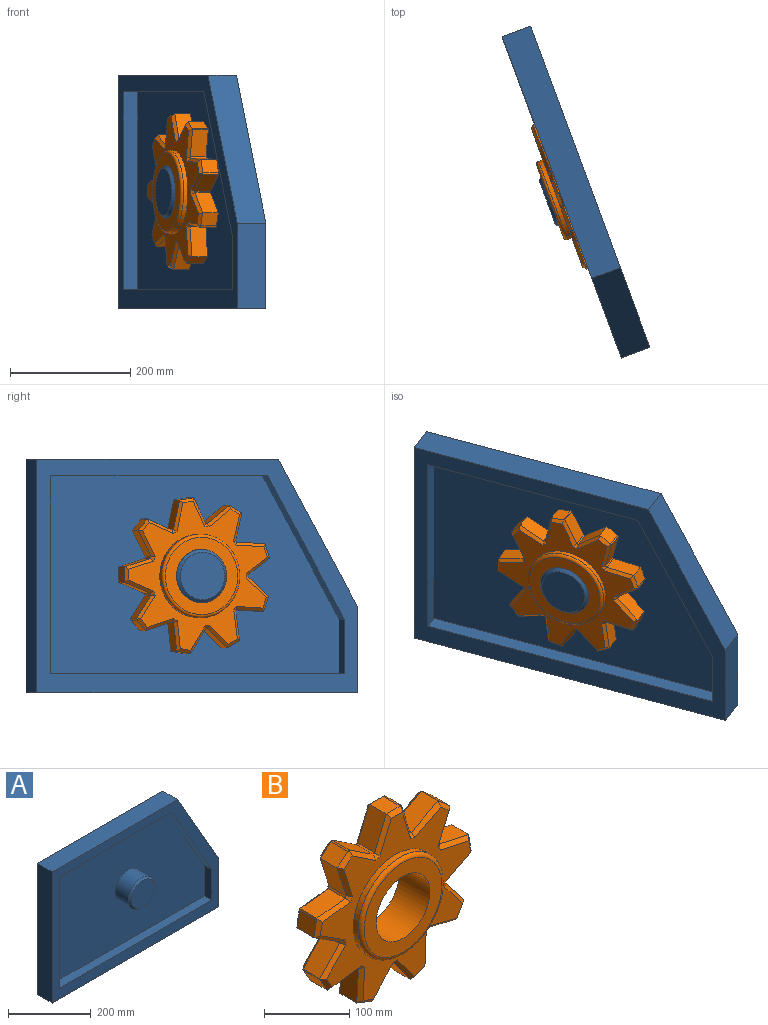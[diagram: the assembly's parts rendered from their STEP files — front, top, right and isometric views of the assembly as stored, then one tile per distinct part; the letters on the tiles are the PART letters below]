
ASSEMBLY  parts=2 mates=1
PART A: 16 faces, bbox 569.8x76.2x388.2 mm
  f0: plane 569.83x388.19mm, normal (0,1,0), area 203883.7mm2, adj f6,f7,f8,f9,f10
  f1: plane 384.89x25.4mm, normal (0,0,-1), area 9776.1mm2, adj f2,f5,f11,f12
  f2: plane 329.12x25.4mm, normal (1,0,0), area 8359.7mm2, adj f1,f3,f11,f12
  f3: plane 521.46x25.4mm, normal (0,0,1), area 13245.1mm2, adj f2,f4,f11,f12
  f4: plane 90.86x25.4mm, normal (-1,0,0), area 2307.9mm2, adj f3,f5,f11,f12
  f5: plane 238.26x136.58mm, normal (-0.87,0,-0.5), area 6975.6mm2, adj f1,f4,f11,f12
  f6: plane 428.93x50.8mm, normal (0,0,1), area 21789.7mm2, adj f0,f7,f10,f11
  f7: plane 388.19x50.8mm, normal (-1,0,0), area 19719.8mm2, adj f0,f6,f8,f11
  f8: plane 569.83x50.8mm, normal (0,0,-1), area 28947.5mm2, adj f0,f7,f9,f11
  f9: plane 142.38x50.8mm, normal (1,0,0), area 7233mm2, adj f0,f8,f10,f11
  f10: plane 245.8x140.9mm, normal (0.87,0,0.5), area 14392.8mm2, adj f0,f6,f9,f11
  f11: plane 569.83x388.19mm, normal (0,-1,0), area 48530.3mm2, adj f1,f2,f3,f4,f5,f6,f7,f8
  f12: plane 521.46x329.12mm, normal (0,-1,0), area 149146.3mm2, adj f1,f2,f3,f4,f5,f13
  f13: cylinder r=44.45mm len=88.9mm, axis (0,1,0), area 12769mm2, adj f12,f15
  f14: plane 78.74x78.74mm, normal (0,-1,0), area 4869.5mm2, adj f15
  f15: cone r=39.37mm half-angle=45deg, axis (0,1,0), area 1891.8mm2, adj f13,f14
PART B: 123 faces, bbox 260x50.8x257 mm
  f0: cylinder r=88.9mm len=27.94mm, axis (0,1,0), area 84mm2, adj f1,f44,f71,f107
  f1: plane 42.39x27.94mm, normal (0.45,0,-0.89), area 1323.4mm2, adj f0,f2,f73,f109
  f2: cylinder r=130.4mm len=28.36mm, axis (0,1,0), area 67.7mm2, adj f1,f3,f73,f75,f109,f111
  f3: plane 27.94x22.84mm, normal (0.99,0,0.16), area 646.6mm2, adj f2,f4,f75,f111
  f4: plane 48.59x27.94mm, normal (0.22,0,0.98), area 1390.3mm2, adj f3,f5,f77,f113
  f5: cylinder r=88.9mm len=27.94mm, axis (0,1,0), area 84mm2, adj f4,f6,f79,f115
  f6: plane 43.44x27.94mm, normal (0.92,0,-0.4), area 1323.4mm2, adj f5,f7,f81,f117
  f7: cylinder r=130.4mm len=28.36mm, axis (0,1,0), area 67.7mm2, adj f6,f8,f81,f82,f117,f118
  f8: plane 27.94x17.55mm, normal (0.65,0,0.76), area 646.6mm2, adj f7,f9,f82,f118
  f9: plane 44.11x27.94mm, normal (-0.46,0,0.89), area 1390.3mm2, adj f8,f10,f80,f116
  f10: cylinder r=88.9mm len=27.94mm, axis (0,1,0), area 84mm2, adj f9,f11,f78,f114
  f11: plane 45.42x27.94mm, normal (0.96,0,0.28), area 1323.4mm2, adj f10,f12,f76,f112
  f12: cylinder r=130.4mm len=28.36mm, axis (0,1,0), area 67.7mm2, adj f11,f13,f74,f76,f110,f112
  f13: plane 27.94x23.14mm, normal (0.01,0,1), area 646.6mm2, adj f12,f14,f74,f110
  f14: plane 45.99x27.94mm, normal (-0.92,0,0.38), area 1390.3mm2, adj f13,f15,f72,f108
  f15: cylinder r=88.9mm len=27.94mm, axis (0,1,0), area 84mm2, adj f14,f16,f70,f106
  f16: plane 39.5x27.94mm, normal (0.55,0,0.83), area 1323.4mm2, adj f15,f17,f68,f104
  f17: cylinder r=130.4mm len=28.36mm, axis (0,1,0), area 67.7mm2, adj f16,f18,f66,f68,f102,f104
  f18: plane 27.94x17.9mm, normal (-0.63,0,0.77), area 646.6mm2, adj f17,f19,f66,f102
  f19: plane 47.44x27.94mm, normal (-0.95,0,-0.3), area 1390.3mm2, adj f18,f20,f64,f100
  f20: cylinder r=88.9mm len=27.94mm, axis (0,1,0), area 84mm2, adj f19,f21,f62,f98
  f21: plane 47.06x27.94mm, normal (-0.11,0,0.99), area 1323.4mm2, adj f20,f22,f60,f96
  f22: cylinder r=130.4mm len=28.36mm, axis (0,1,0), area 67.7mm2, adj f21,f23,f58,f60,f94,f96
  f23: plane 27.94x22.74mm, normal (-0.98,0,0.19), area 646.6mm2, adj f22,f24,f58,f94
  f24: plane 41.99x27.94mm, normal (-0.54,0,-0.84), area 1390.3mm2, adj f23,f25,f56,f92
  f25: cylinder r=88.9mm len=27.94mm, axis (0,1,0), area 84mm2, adj f24,f26,f54,f90
  f26: plane 34.36x32.61mm, normal (-0.73,0,0.69), area 1323.4mm2, adj f25,f27,f52,f88
  f27: cylinder r=130.4mm len=28.36mm, axis (0,1,0), area 67.7mm2, adj f26,f28,f50,f52,f86,f88
  f28: plane 27.94x20.18mm, normal (-0.87,0,-0.49), area 646.6mm2, adj f27,f29,f50,f86
  f29: plane 49.33x27.94mm, normal (0.13,0,-0.99), area 1390.3mm2, adj f28,f30,f48,f84
  f30: cylinder r=88.9mm len=27.94mm, axis (0,1,0), area 84mm2, adj f29,f31,f47,f83
  f31: plane 47.28x27.94mm, normal (-1,0,0.06), area 1323.4mm2, adj f30,f32,f49,f85
  f32: cylinder r=130.4mm len=28.36mm, axis (0,1,0), area 67.7mm2, adj f31,f33,f49,f51,f85,f87
  f33: plane 27.94x21.65mm, normal (-0.35,0,-0.94), area 646.6mm2, adj f32,f34,f51,f87
  f34: plane 36.72x33.58mm, normal (0.74,0,-0.67), area 1390.3mm2, adj f33,f35,f53,f89
  f35: cylinder r=88.9mm len=27.94mm, axis (0,1,0), area 84mm2, adj f34,f36,f55,f91
  f36: plane 38.08x28.17mm, normal (-0.8,0,-0.59), area 1323.4mm2, adj f35,f37,f57,f93
  f37: cylinder r=130.4mm len=28.36mm, axis (0,1,0), area 67.7mm2, adj f36,f38,f57,f59,f93,f95
  f38: plane 27.94x21.84mm, normal (0.33,0,-0.94), area 646.6mm2, adj f37,f39,f59,f95
  f39: plane 49.71x27.94mm, normal (1,0,-0.04), area 1390.3mm2, adj f38,f40,f61,f97
  f40: cylinder r=88.9mm len=27.94mm, axis (0,1,0), area 84mm2, adj f39,f41,f63,f99
  f41: plane 46.06x27.94mm, normal (-0.23,0,-0.97), area 1323.4mm2, adj f40,f42,f65,f101
  f42: cylinder r=130.4mm len=28.36mm, axis (0,1,0), area 67.7mm2, adj f41,f43,f65,f67,f101,f103
  f43: plane 27.94x19.91mm, normal (0.86,0,-0.51), area 646.6mm2, adj f42,f44,f67,f103
  f44: plane 39.45x30.33mm, normal (0.79,0,0.61), area 1390.3mm2, adj f0,f43,f69,f105
  f45: plane 248.95x246.02mm, normal (0,-1,0), area 19557.7mm2, adj f47,f48,f49,f50,f51,f52,f53,f54
  f46: plane 248.95x246.02mm, normal (0,1,0), area 28484.4mm2, adj f83,f84,f85,f86,f87,f88,f89,f90
  f47: cone r=83.82mm half-angle=45deg, axis (0,1,0), area 38.5mm2, adj f30,f45,f48,f49
  f48: plane 50.97x11.89mm, normal (0.09,-0.71,-0.7), area 353.4mm2, adj f29,f45,f47,f50
  f49: plane 49.73x8.13mm, normal (-0.71,-0.71,0.04), area 338.1mm2, adj f31,f32,f45,f47,f51
  f50: plane 22.18x14.97mm, normal (-0.62,-0.71,-0.35), area 156.8mm2, adj f27,f28,f45,f48,f52
  f51: plane 23.61x12.43mm, normal (-0.25,-0.71,-0.66), area 156.8mm2, adj f32,f33,f45,f49,f53
  f52: plane 38.13x35.31mm, normal (-0.51,-0.71,0.49), area 338.1mm2, adj f26,f27,f45,f50,f54
  f53: plane 41.87x35.01mm, normal (0.52,-0.71,-0.48), area 353.4mm2, adj f34,f45,f51,f55
  f54: cone r=83.82mm half-angle=45deg, axis (0,1,0), area 38.5mm2, adj f25,f45,f52,f56
  f55: cone r=83.82mm half-angle=45deg, axis (0,1,0), area 38.5mm2, adj f35,f45,f53,f57
  f56: plane 46.68x29.13mm, normal (-0.38,-0.71,-0.6), area 353.4mm2, adj f24,f45,f54,f58
  f57: plane 43.24x30.17mm, normal (-0.57,-0.71,-0.42), area 338.1mm2, adj f36,f37,f45,f55,f59
  f58: plane 24.84x9.02mm, normal (-0.69,-0.71,0.13), area 156.8mm2, adj f22,f23,f45,f56,f60
  f59: plane 23.96x11.84mm, normal (0.23,-0.71,-0.67), area 156.8mm2, adj f37,f38,f45,f57,f61
  f60: plane 50.35x10.01mm, normal (-0.08,-0.71,0.7), area 338.1mm2, adj f21,f22,f45,f58,f62
  f61: plane 52.26x7.05mm, normal (0.71,-0.71,-0.03), area 353.4mm2, adj f39,f45,f59,f63
  f62: cone r=83.82mm half-angle=45deg, axis (0,1,0), area 38.5mm2, adj f20,f45,f60,f64
  f63: cone r=83.82mm half-angle=45deg, axis (0,1,0), area 38.5mm2, adj f40,f45,f61,f65
  f64: plane 48.13x20.56mm, normal (-0.67,-0.71,-0.21), area 353.4mm2, adj f19,f45,f62,f66
  f65: plane 47.6x16.62mm, normal (-0.17,-0.71,-0.69), area 338.1mm2, adj f41,f42,f45,f63,f67
  f66: plane 20.03x17.63mm, normal (-0.45,-0.71,0.55), area 156.8mm2, adj f17,f18,f45,f64,f68
  f67: plane 21.67x15.46mm, normal (0.61,-0.71,-0.36), area 156.8mm2, adj f42,f43,f45,f65,f69
  f68: plane 39.69x31.85mm, normal (0.39,-0.71,0.59), area 338.1mm2, adj f16,f17,f45,f66,f70
  f69: plane 39.81x35.78mm, normal (0.56,-0.71,0.43), area 353.4mm2, adj f44,f45,f67,f71
  f70: cone r=83.82mm half-angle=45deg, axis (0,1,0), area 38.5mm2, adj f15,f45,f68,f72
  f71: cone r=83.82mm half-angle=45deg, axis (0,1,0), area 38.5mm2, adj f0,f45,f69,f73
  f72: plane 50.08x22.38mm, normal (-0.65,-0.71,0.27), area 353.4mm2, adj f14,f45,f70,f74
  f73: plane 47.04x24.12mm, normal (0.32,-0.71,-0.63), area 338.1mm2, adj f1,f2,f45,f71,f75
  f74: plane 25.31x5.34mm, normal (0.01,-0.71,0.71), area 156.8mm2, adj f12,f13,f45,f72,f76
  f75: plane 25.02x8.36mm, normal (0.7,-0.71,0.11), area 156.8mm2, adj f2,f3,f45,f73,f77
  f76: plane 49.44x17.33mm, normal (0.68,-0.71,0.2), area 338.1mm2, adj f11,f12,f45,f74,f78
  f77: plane 51.96x14.94mm, normal (0.15,-0.71,0.69), area 353.4mm2, adj f4,f45,f75,f79
  f78: cone r=83.82mm half-angle=45deg, axis (0,1,0), area 38.5mm2, adj f10,f45,f76,f80
  f79: cone r=83.82mm half-angle=45deg, axis (0,1,0), area 38.5mm2, adj f5,f45,f77,f81
  f80: plane 44.11x28.6mm, normal (-0.33,-0.71,0.63), area 353.4mm2, adj f9,f45,f78,f82
  f81: plane 44.02x24.61mm, normal (0.65,-0.71,-0.28), area 338.1mm2, adj f6,f7,f45,f79,f82
  f82: plane 19.77x18.01mm, normal (0.46,-0.71,0.54), area 156.8mm2, adj f7,f8,f45,f80,f81
  f83: cone r=88.9mm half-angle=45deg, axis (0,-1,0), area 38.5mm2, adj f30,f46,f84,f85
  f84: plane 50.97x11.89mm, normal (0.09,0.71,-0.7), area 353.4mm2, adj f29,f46,f83,f86
  f85: plane 49.73x8.13mm, normal (-0.71,0.71,0.04), area 338.1mm2, adj f31,f32,f46,f83,f87
  f86: plane 22.18x14.97mm, normal (-0.62,0.71,-0.35), area 156.8mm2, adj f27,f28,f46,f84,f88
  f87: plane 23.61x12.43mm, normal (-0.25,0.71,-0.66), area 156.8mm2, adj f32,f33,f46,f85,f89
  f88: plane 38.13x35.31mm, normal (-0.51,0.71,0.49), area 338.1mm2, adj f26,f27,f46,f86,f90
  f89: plane 41.87x35.01mm, normal (0.52,0.71,-0.48), area 353.4mm2, adj f34,f46,f87,f91
  f90: cone r=88.9mm half-angle=45deg, axis (0,-1,0), area 38.5mm2, adj f25,f46,f88,f92
  f91: cone r=88.9mm half-angle=45deg, axis (0,-1,0), area 38.5mm2, adj f35,f46,f89,f93
  f92: plane 46.68x29.13mm, normal (-0.38,0.71,-0.6), area 353.4mm2, adj f24,f46,f90,f94
  f93: plane 43.24x30.17mm, normal (-0.57,0.71,-0.42), area 338.1mm2, adj f36,f37,f46,f91,f95
  f94: plane 24.84x9.02mm, normal (-0.69,0.71,0.13), area 156.8mm2, adj f22,f23,f46,f92,f96
  f95: plane 23.96x11.84mm, normal (0.23,0.71,-0.67), area 156.8mm2, adj f37,f38,f46,f93,f97
  f96: plane 50.35x10.01mm, normal (-0.08,0.71,0.7), area 338.1mm2, adj f21,f22,f46,f94,f98
  f97: plane 52.26x7.05mm, normal (0.71,0.71,-0.03), area 353.4mm2, adj f39,f46,f95,f99
  f98: cone r=88.9mm half-angle=45deg, axis (0,-1,0), area 38.5mm2, adj f20,f46,f96,f100
  f99: cone r=88.9mm half-angle=45deg, axis (0,-1,0), area 38.5mm2, adj f40,f46,f97,f101
  f100: plane 48.13x20.56mm, normal (-0.67,0.71,-0.21), area 353.4mm2, adj f19,f46,f98,f102
  f101: plane 47.6x16.62mm, normal (-0.17,0.71,-0.69), area 338.1mm2, adj f41,f42,f46,f99,f103
  f102: plane 20.03x17.63mm, normal (-0.45,0.71,0.55), area 156.8mm2, adj f17,f18,f46,f100,f104
  f103: plane 21.67x15.46mm, normal (0.61,0.71,-0.36), area 156.8mm2, adj f42,f43,f46,f101,f105
  f104: plane 39.69x31.85mm, normal (0.39,0.71,0.59), area 338.1mm2, adj f16,f17,f46,f102,f106
  f105: plane 39.81x35.78mm, normal (0.56,0.71,0.43), area 353.4mm2, adj f44,f46,f103,f107
  f106: cone r=88.9mm half-angle=45deg, axis (0,-1,0), area 38.5mm2, adj f15,f46,f104,f108
  f107: cone r=88.9mm half-angle=45deg, axis (0,-1,0), area 38.5mm2, adj f0,f46,f105,f109
  f108: plane 50.08x22.38mm, normal (-0.65,0.71,0.27), area 353.4mm2, adj f14,f46,f106,f110
  f109: plane 47.04x24.12mm, normal (0.32,0.71,-0.63), area 338.1mm2, adj f1,f2,f46,f107,f111
  f110: plane 25.31x5.34mm, normal (0.01,0.71,0.71), area 156.8mm2, adj f12,f13,f46,f108,f112
  f111: plane 25.02x8.36mm, normal (0.7,0.71,0.11), area 156.8mm2, adj f2,f3,f46,f109,f113
  f112: plane 49.44x17.33mm, normal (0.68,0.71,0.2), area 338.1mm2, adj f11,f12,f46,f110,f114
  f113: plane 51.96x14.94mm, normal (0.15,0.71,0.69), area 353.4mm2, adj f4,f46,f111,f115
  f114: cone r=88.9mm half-angle=45deg, axis (0,-1,0), area 38.5mm2, adj f10,f46,f112,f116
  f115: cone r=88.9mm half-angle=45deg, axis (0,-1,0), area 38.5mm2, adj f5,f46,f113,f117
  f116: plane 44.11x28.6mm, normal (-0.33,0.71,0.63), area 353.4mm2, adj f9,f46,f114,f118
  f117: plane 44.02x24.61mm, normal (0.65,0.71,-0.28), area 338.1mm2, adj f6,f7,f46,f115,f118
  f118: plane 19.77x18.01mm, normal (0.46,0.71,0.54), area 156.8mm2, adj f7,f8,f46,f116,f117
  f119: cylinder r=69.41mm len=138.81mm, axis (0,1,0), area 3323mm2, adj f45,f121
  f120: plane 128.65x128.65mm, normal (0,-1,0), area 6792.5mm2, adj f121,f122
  f121: torus R=64.33mm, axis (0,-1,0), area 3387.3mm2, adj f119,f120
  f122: cylinder r=44.45mm len=88.9mm, axis (0,1,0), area 14187.8mm2, adj f46,f120
PLACE A rot(axis=(0,0,-1),69.6deg) t=(462.33,349.28,-306.84)mm
PLACE B rot(axis=(0.44,0.64,-0.63),95.4deg) t=(443.28,342.21,-306.84)mm
MATE revolute A.f13 <-> B.f122  axis (0.94,0.35,0) through (395.66,324.53,-306.84)mm
